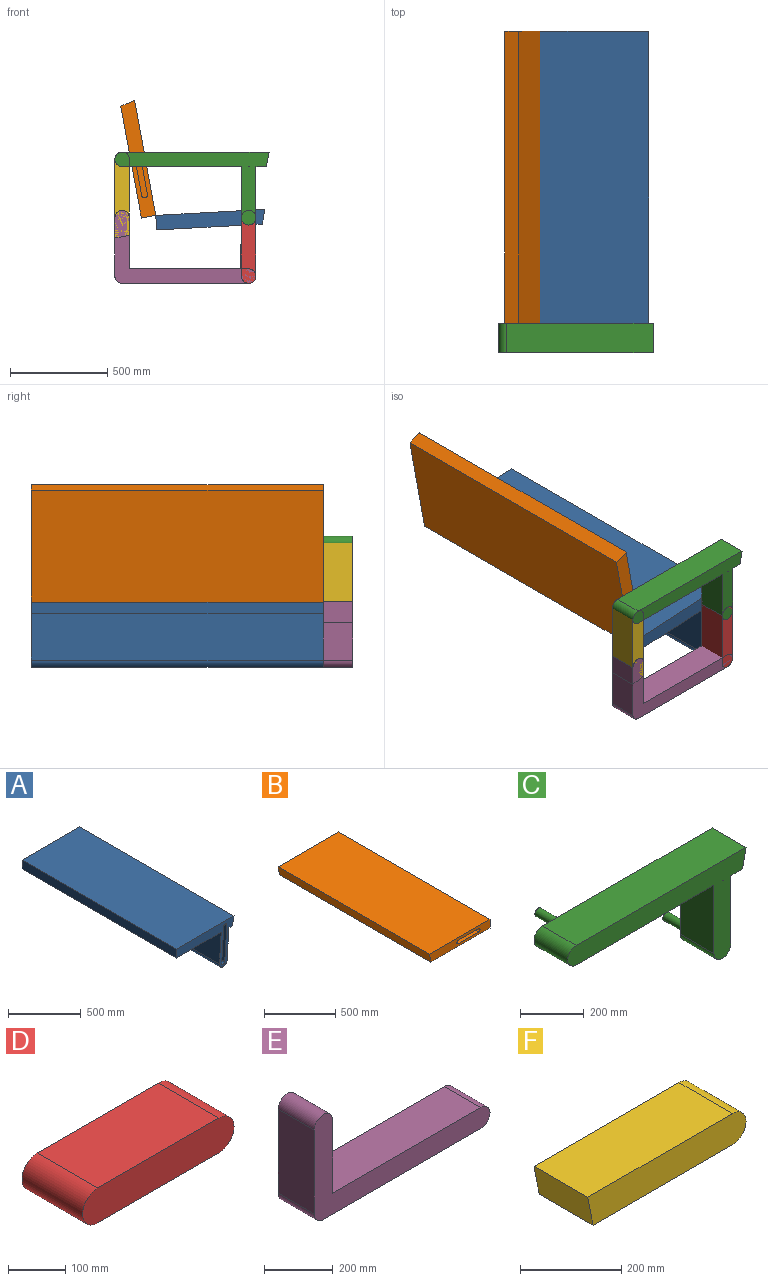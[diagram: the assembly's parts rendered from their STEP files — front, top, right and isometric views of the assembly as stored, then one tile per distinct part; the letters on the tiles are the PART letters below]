
ASSEMBLY  parts=6 mates=7
PART A: 15 faces, bbox 560x1500x375 mm
  f0: plane 1500x435.76mm, normal (0,0,-1), area 653646.3mm2, adj f1,f2,f6,f7
  f1: plane 560x375mm, normal (0,-1,0), area 53675.1mm2, adj f0,f2,f3,f4,f5,f7,f8,f9
  f2: plane 1500x75mm, normal (-1,0,0), area 112500mm2, adj f0,f1,f5,f6
  f3: plane 1500x34.05mm, normal (0,0,-1), area 51079mm2, adj f1,f4,f6,f9
  f4: plane 1500x75mm, normal (0.98,0,-0.2), area 114727.9mm2, adj f1,f3,f5,f6
  f5: plane 1500x560mm, normal (0,0,1), area 840000mm2, adj f1,f2,f4,f6
  f6: plane 560x375mm, normal (0,1,0), area 63382mm2, adj f0,f2,f3,f4,f5,f7,f8,f9
  f7: plane 1500x259.88mm, normal (-1,0,0.07), area 390778.1mm2, adj f0,f1,f6,f8
  f8: cylinder r=37.5mm len=1500mm, axis (0,-1,0), area 176714.6mm2, adj f1,f6,f7,f9
  f9: plane 1500x265.12mm, normal (1,0,-0.07), area 398644.9mm2, adj f1,f3,f6,f8
  f10: plane 299.27x100mm, normal (-1,0,0.07), area 30000mm2, adj f1,f11,f13,f14
  f11: cylinder r=15mm len=100mm, axis (0,-1,0), area 4712.4mm2, adj f1,f10,f12,f14
  f12: plane 299.27x100mm, normal (1,0,-0.07), area 30000mm2, adj f1,f11,f13,f14
  f13: cylinder r=15mm len=100mm, axis (0,-1,0), area 4712.4mm2, adj f1,f10,f12,f14
  f14: plane 329.27x50.93mm, normal (0,-1,0), area 9706.9mm2, adj f10,f11,f12,f13
PART B: 11 faces, bbox 600x1500x75 mm
  f0: plane 1500x600mm, normal (0,0,1), area 900000mm2, adj f1,f3,f4,f5
  f1: plane 1500x75mm, normal (-0.98,0,-0.2), area 114727.9mm2, adj f0,f2,f4,f5
  f2: plane 1500x585mm, normal (0,0,-1), area 877500mm2, adj f1,f3,f4,f5
  f3: plane 1500x75mm, normal (1,0,0), area 112500mm2, adj f0,f2,f4,f5
  f4: plane 600x75mm, normal (0,1,0), area 44437.5mm2, adj f0,f1,f2,f3
  f5: plane 600x75mm, normal (0,-1,0), area 37756.1mm2, adj f0,f1,f2,f3,f6,f7,f8,f9
  f6: plane 199.15x100mm, normal (0,0,-1), area 19915.1mm2, adj f5,f7,f9,f10
  f7: cylinder r=15mm len=100mm, axis (0,-1,0), area 4712.4mm2, adj f5,f6,f8,f10
  f8: plane 199.15x100mm, normal (0,0,1), area 19915.1mm2, adj f5,f7,f9,f10
  f9: cylinder r=15mm len=100mm, axis (0,-1,0), area 4712.4mm2, adj f5,f6,f8,f10
  f10: plane 229.15x30mm, normal (0,-1,0), area 6681.4mm2, adj f6,f7,f8,f9
PART C: 17 faces, bbox 792.5x250x375 mm
  f0: plane 150x3.32mm, normal (0,0,1), area 497.9mm2, adj f1,f10,f11,f12
  f1: cylinder r=37.5mm len=150mm, axis (0,1,0), area 500.1mm2, adj f0,f10,f11,f12
  f2: plane 755x150mm, normal (0,0,1), area 113250mm2, adj f3,f9,f11,f12
  f3: cylinder r=37.5mm len=150mm, axis (0,1,0), area 17671.5mm2, adj f2,f4,f11,f12
  f4: plane 612.5x150mm, normal (0,0,-1), area 91875mm2, adj f3,f5,f11,f12
  f5: plane 262.5x150mm, normal (-1,0,0), area 39375mm2, adj f4,f6,f11,f12
  f6: cylinder r=37.5mm len=150mm, axis (0,1,0), area 17671.5mm2, adj f5,f7,f11,f12
  f7: plane 262.5x150mm, normal (1,0,0), area 39375mm2, adj f6,f8,f11,f12
  f8: plane 150x52.5mm, normal (0,0,-1), area 7875mm2, adj f7,f9,f11,f12
  f9: plane 150x75mm, normal (0.98,0,-0.2), area 11472.8mm2, adj f2,f8,f11,f12
  f10: plane 150x0.15mm, normal (-1,0,0.07), area 22.3mm2, adj f0,f1,f11,f12
  f11: plane 792.5x375mm, normal (0,-1,0), area 80167.7mm2, adj f0,f1,f2,f3,f4,f5,f6,f7
  f12: plane 792.5x375mm, normal (0,1,0), area 78754mm2, adj f0,f1,f2,f3,f4,f5,f6,f7
  f13: cylinder r=15mm len=100mm, axis (0,-1,0), area 9424.8mm2, adj f12,f14
  f14: plane 30x30mm, normal (0,1,0), area 706.9mm2, adj f13
  f15: cylinder r=15mm len=100mm, axis (0,-1,0), area 9424.8mm2, adj f12,f16
  f16: plane 30x30mm, normal (0,1,0), area 706.9mm2, adj f15
PART D: 6 faces, bbox 375x150x75 mm
  f0: plane 300x150mm, normal (0,0,-1), area 45000mm2, adj f1,f3,f4,f5
  f1: cylinder r=37.5mm len=150mm, axis (0,1,0), area 17671.5mm2, adj f0,f2,f4,f5
  f2: plane 300x150mm, normal (0,0,1), area 45000mm2, adj f1,f3,f4,f5
  f3: cylinder r=37.5mm len=150mm, axis (0,1,0), area 17671.5mm2, adj f0,f2,f4,f5
  f4: plane 375x75mm, normal (0,-1,0), area 26917.9mm2, adj f0,f1,f2,f3
  f5: plane 375x75mm, normal (0,1,0), area 26917.9mm2, adj f0,f1,f2,f3
PART E: 9 faces, bbox 725x150x375 mm
  f0: plane 262.5x150mm, normal (1,0,0), area 39375mm2, adj f1,f6,f7,f8
  f1: cylinder r=37.5mm len=150mm, axis (0,1,0), area 17671.5mm2, adj f0,f2,f7,f8
  f2: plane 300x150mm, normal (-1,0,0), area 45000mm2, adj f1,f3,f7,f8
  f3: cylinder r=37.5mm len=150mm, axis (0,1,0), area 8835.7mm2, adj f2,f4,f7,f8
  f4: plane 650x150mm, normal (0,0,-1), area 97500mm2, adj f3,f5,f7,f8
  f5: cylinder r=37.5mm len=150mm, axis (0,1,0), area 17671.5mm2, adj f4,f6,f7,f8
  f6: plane 612.5x150mm, normal (0,0,1), area 91875mm2, adj f0,f5,f7,f8
  f7: plane 725x375mm, normal (0,-1,0), area 75366.1mm2, adj f0,f1,f2,f3,f4,f5,f6
  f8: plane 725x375mm, normal (0,1,0), area 75366.1mm2, adj f0,f1,f2,f3,f4,f5,f6
PART F: 6 faces, bbox 442.5x150x75 mm
  f0: cylinder r=37.5mm len=150mm, axis (0,1,0), area 17671.5mm2, adj f1,f3,f4,f5
  f1: plane 405x150mm, normal (0,0,1), area 60750mm2, adj f0,f2,f4,f5
  f2: plane 150x75mm, normal (-0.98,0,-0.2), area 11472.8mm2, adj f1,f3,f4,f5
  f3: plane 390x150mm, normal (0,0,-1), area 58500mm2, adj f0,f2,f4,f5
  f4: plane 442.5x75mm, normal (0,-1,0), area 32021.4mm2, adj f0,f1,f2,f3
  f5: plane 442.5x75mm, normal (0,1,0), area 32021.4mm2, adj f0,f1,f2,f3
PLACE A rot(axis=(0,-1,0),3.1deg) t=(-250.57,0,-7.68)mm
PLACE B rot(axis=(0,1,0),79.6deg) t=(-1851.77,0,769.2)mm
PLACE C rot(axis=(0,1,0),0deg) t=(-300,0,300)mm fixed
PLACE D rot(axis=(0,-1,0),90deg) t=(846.03,0,1110.92)mm
PLACE E at identity fixed
PLACE F rot(axis=(0,-1,0),90deg) t=(496.03,0,2060.92)mm
MATE revolute C.f6 <-> D.f1  axis (0,-1,0) through (-132.44,-150,1278.47)mm
MATE pin_slot C.f6 <-> A.f8  axis (0,1,0) through (-132.44,100,1278.47)mm
MATE revolute F.f4 <-> E.f1  axis (0,-1,0) through (-782.44,-150,1278.47)mm
MATE revolute F.f0 <-> C.f3  axis (0,-1,0) through (-782.44,-150,1578.47)mm
MATE revolute A.f1 <-> B.f5  axis (0,-1,0) through (-609.75,0,1290.55)mm
MATE pin_slot C.f13 <-> B.f7  axis (0,1,0) through (-700.98,100,1578.47)mm
MATE revolute D.f3 <-> E.f5  axis (0,-1,0) through (-132.44,-150,978.47)mm
